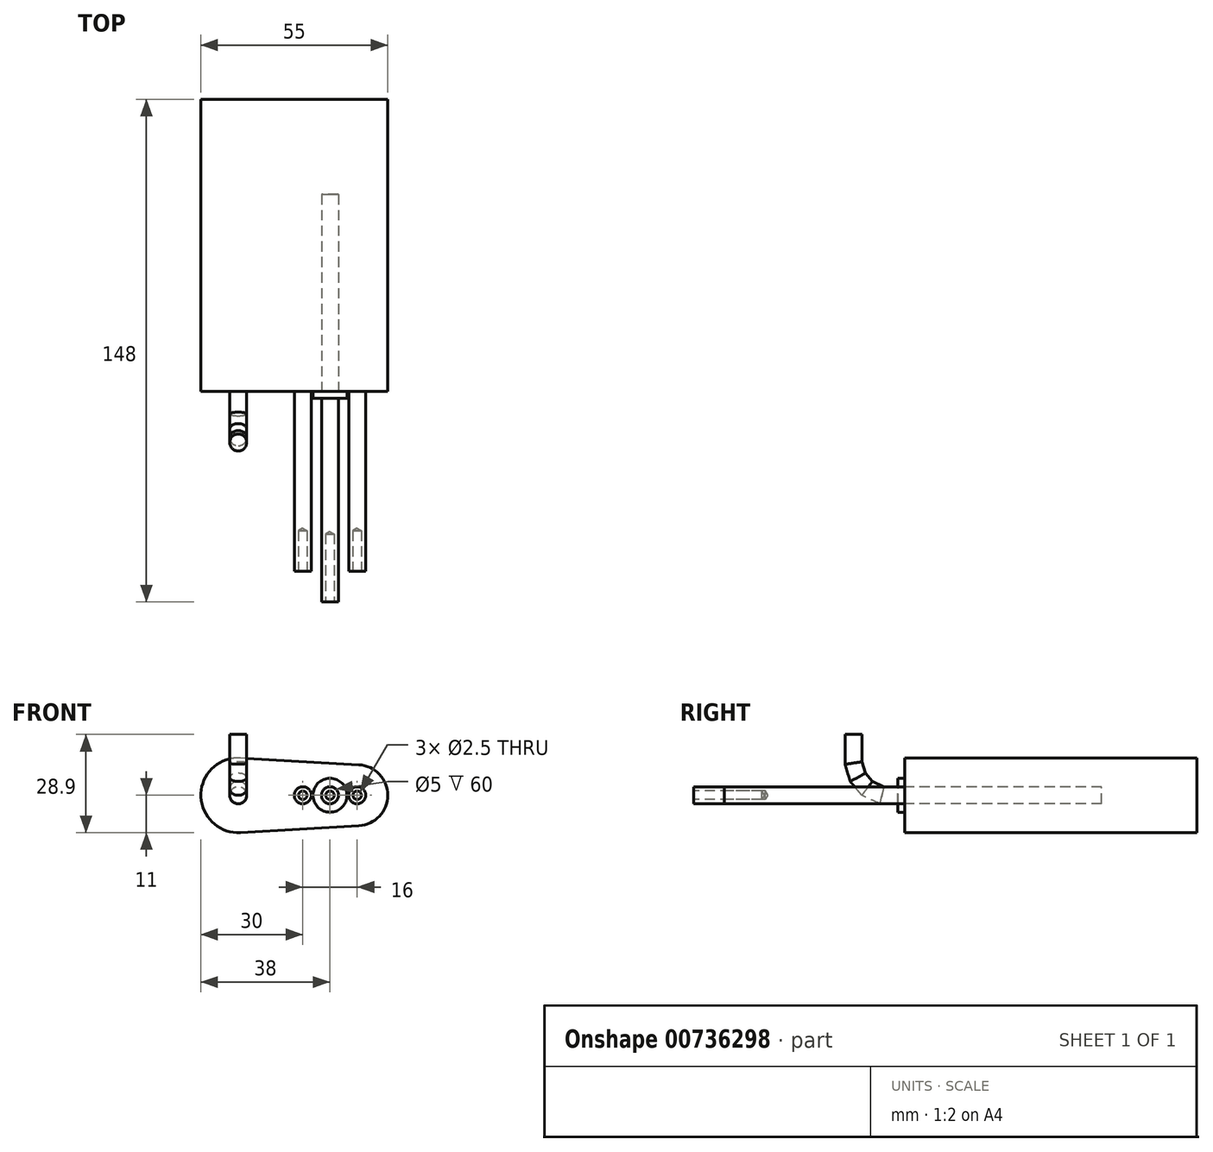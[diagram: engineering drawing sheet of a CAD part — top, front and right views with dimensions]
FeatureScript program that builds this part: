
annotation { "Feature Type Name" : "Feature", "Feature Type Description" : "" }
export const myFeature = defineFeature(function(context is Context, id is Id, definition is map)
    precondition{}
    {
        {
            var Q0;
            Q0=qCreatedBy(makeId("Front.planeOp"),FACE);
            var sketch = newSketch(context, id + "F0", { "sketchPlane" : qUnion([Q0])});
            skCircle(sketch, "E0", {"center": v(0, 0) * mm, "radius": 11 * mm});
            skCircle(sketch, "E1", {"center": v(35, 0) * mm, "radius": 9 * mm});
            skLineSegment(sketch, "E2", {"start": v(35.51, 8.99) * mm, "end": v(0.63, 10.98) * mm});
            skLineSegment(sketch, "E3", {"start": v(0.63, -10.98) * mm, "end": v(35.51, -8.99) * mm});
            skSolve(sketch);
        }
        {
            var Q0;
            Q0 = qSketchRegion(id + "F0", true);
            extrude(context, id + "F1", {"entities" : qUnion([Q0]), "depth" : 86 * mm, "offsetDistance" : 25 * mm});
        }
        {
            var Q0;
            Q0=makeQuery(id+"F1.opExtrude","CAP_FACE",FACE,{"disambiguationData":[OSD([sQuery(id+"F0.wireOp",EDGE,"E0"),sQuery(id+"F0.wireOp",EDGE,"E1"),sQuery(id+"F0.wireOp",EDGE,"E2"),sQuery(id+"F0.wireOp",EDGE,"E3")])],"isStart":false});
            var sketch = newSketch(context, id + "F2", { "sketchPlane" : qUnion([Q0])});
            skCircle(sketch, "E4", {"center": v(35, 0) * mm, "radius": 2.5 * mm});
            skCircle(sketch, "E5", {"center": v(19, 0) * mm, "radius": 2.5 * mm});
            skCircle(sketch, "E6", {"center": v(27, 0) * mm, "radius": 5 * mm});
            skLineSegment(sketch, "E7", {"start": v(27, 0) * mm, "end": v(35, 0) * mm, "construction": true});
            skLineSegment(sketch, "E8", {"start": v(27, 0) * mm, "end": v(19, 0) * mm, "construction": true});
            skCircle(sketch, "E9", {"center": v(0, 0) * mm, "radius": 2.5 * mm});
            skSolve(sketch);
        }
        {
            var Q0;
            Q0=makeQuery(id+"F2.imprint","IMPRINT",FACE,{"disambiguationData":[TD([[makeQuery(id+"F2.imprint","IMPRINT",EDGE,{"derivedFrom":sQuery(id+"F2.wireOp",EDGE,"E6")}),1.0]])]});
            extrude(context, id + "F3", {"entities" : qUnion([Q0]), "operationType" : NewBodyOperationType.ADD, "depth" : 2 * mm, "offsetDistance" : 25 * mm});
        }
        {
            var Q0;
            Q0=makeQuery(id+"F2.imprint","IMPRINT",FACE,{"disambiguationData":[TD([[makeQuery(id+"F2.imprint","IMPRINT",EDGE,{"derivedFrom":sQuery(id+"F2.wireOp",EDGE,"E5")}),1.0]])]});
            var Q1;
            Q1=makeQuery(id+"F2.imprint","IMPRINT",FACE,{"disambiguationData":[TD([[makeQuery(id+"F2.imprint","IMPRINT",EDGE,{"derivedFrom":sQuery(id+"F2.wireOp",EDGE,"E4")}),1.0]])]});
            extrude(context, id + "F4", {"entities" : qUnion([Q0, Q1]), "operationType" : NewBodyOperationType.ADD, "depth" : 53 * mm, "offsetDistance" : 25 * mm});
        }
        {
            var Q0;
            Q0=makeQuery(id+"F3.opExtrude","CAP_FACE",FACE,{"disambiguationData":[OSD([sQuery(id+"F2.wireOp",EDGE,"E6")])],"isStart":false});
            var sketch = newSketch(context, id + "F5", { "sketchPlane" : qUnion([Q0])});
            skCircle(sketch, "E10", {"center": v(27, 0) * mm, "radius": 2.5 * mm});
            skSolve(sketch);
        }
        {
            var Q0;
            Q0 = qSketchRegion(id + "F5", true);
            extrude(context, id + "F6", {"entities" : qUnion([Q0]), "operationType" : NewBodyOperationType.REMOVE, "oppositeDirection" : true, "depth" : 60 * mm, "offsetDistance" : 25 * mm});
        }
        {
            var Q0;
            Q0 = qSketchRegion(id + "F5", true);
            extrude(context, id + "F7", {"entities" : qUnion([Q0]), "depth" : 60 * mm, "offsetDistance" : 25 * mm});
        }
        {
            var Q0;
            Q0=makeQuery(id+"F4.opExtrude","CAP_FACE",FACE,{"disambiguationData":[OSD([sQuery(id+"F2.wireOp",EDGE,"E5")])],"isStart":false});
            var sketch = newSketch(context, id + "F8", { "sketchPlane" : qUnion([Q0])});
            skPoint(sketch, "E11.0", {"position": v(35, 0) * mm});
            skPoint(sketch, "E11.1", {"position": v(19, 0) * mm});
            skSolve(sketch);
        }
        {
            var Q0;
            Q0=sQuery(id+"F8.wireOp",VERTEX,"E11.1");
            var Q1;
            Q1=sQuery(id+"F8.wireOp",VERTEX,"E11.0");
            var Q2;
            Q2=makeQuery(id+"F1.opExtrude","SWEPT_BODY",BODY,{"disambiguationData":[OSD([sQuery(id+"F0.wireOp",EDGE,"E0"),sQuery(id+"F0.wireOp",EDGE,"E1"),sQuery(id+"F0.wireOp",EDGE,"E2"),sQuery(id+"F0.wireOp",EDGE,"E3")])]});
            hole(context, id + "F9", {"style" : HoleStyle.SIMPLE, "endStyle" : HoleEndStyle.BLIND, "holeDiameter" : 2.5 * mm, "majorDiameter" : 5 * mm, "holeDepth" : 12 * mm, "isTappedThrough" : true, "tappedDepth" : 12 * mm, "tapClearance" : 3, "locations" : qUnion([Q0, Q1]), "scope" : qUnion([Q2])});
        }
        {
            var Q0;
            Q0=makeQuery(id+"F7.opExtrude","CAP_FACE",FACE,{"disambiguationData":[OSD([sQuery(id+"F5.wireOp",EDGE,"E10")])],"isStart":false});
            var sketch = newSketch(context, id + "F10", { "sketchPlane" : qUnion([Q0])});
            skPoint(sketch, "E12.0", {"position": v(27, 0) * mm});
            skSolve(sketch);
        }
        {
            var Q0;
            Q0=sQuery(id+"F10.wireOp",VERTEX,"E12.0");
            var Q1;
            Q1=makeQuery(id+"F7.opExtrude","SWEPT_BODY",BODY,{"disambiguationData":[OSD([sQuery(id+"F5.wireOp",EDGE,"E10")])]});
            hole(context, id + "F11", {"style" : HoleStyle.SIMPLE, "endStyle" : HoleEndStyle.BLIND, "holeDiameter" : 2.5 * mm, "majorDiameter" : 5 * mm, "holeDepth" : 20 * mm, "isTappedThrough" : true, "tappedDepth" : 12 * mm, "tapClearance" : 3, "locations" : qUnion([Q0]), "scope" : qUnion([Q1])});
        }
        {
            var Q0;
            Q0=qCreatedBy(makeId("Right.planeOp"),FACE);
            var sketch = newSketch(context, id + "F12", { "sketchPlane" : qUnion([Q0])});
            skPoint(sketch, "E13.0", {"position": v(-86, 0) * mm});
            skLineSegment(sketch, "E14", {"start": v(-86, 0) * mm, "end": v(-92.64, 0) * mm});
            skLineSegment(sketch, "E15", {"start": v(-92.64, 0) * mm, "end": v(-97.02, 2.01) * mm});
            skLineSegment(sketch, "E16", {"start": v(-97.02, 2.01) * mm, "end": v(-99.74, 5.26) * mm});
            skLineSegment(sketch, "E17", {"start": v(-99.74, 5.26) * mm, "end": v(-101.03, 9.5) * mm});
            skLineSegment(sketch, "E18", {"start": v(-101.03, 9.5) * mm, "end": v(-101.03, 17.9) * mm});
            skSolve(sketch);
        }
        {
            var Q0;
            Q0=makeQuery(id+"F2.imprint","IMPRINT",FACE,{"disambiguationData":[TD([[makeQuery(id+"F2.imprint","IMPRINT",EDGE,{"derivedFrom":sQuery(id+"F2.wireOp",EDGE,"E9")}),1.0]])]});
            var Q1;
            Q1=sQuery(id+"F12.wireOp",EDGE,"E14");
            var Q2;
            Q2=sQuery(id+"F12.wireOp",EDGE,"E15");
            var Q3;
            Q3=sQuery(id+"F12.wireOp",EDGE,"E16");
            var Q4;
            Q4=sQuery(id+"F12.wireOp",EDGE,"E17");
            var Q5;
            Q5=sQuery(id+"F12.wireOp",EDGE,"E18");
            sweep(context, id + "F13", {"operationType" : NewBodyOperationType.ADD, "profiles" : qUnion([Q0]), "path" : qUnion([Q1, Q2, Q3, Q4, Q5])});
        }
    });
